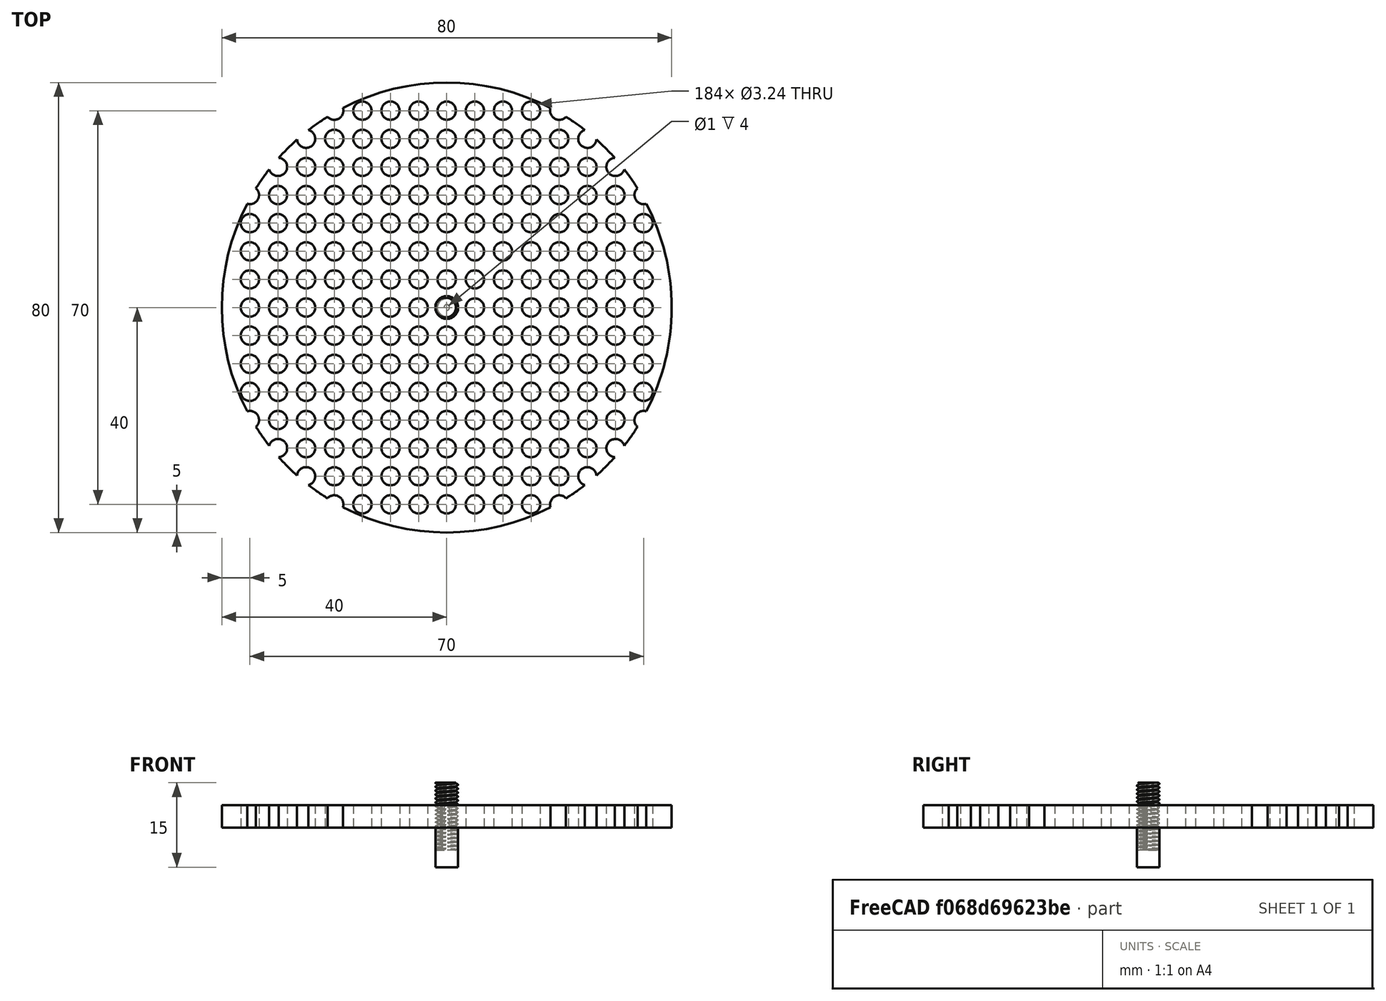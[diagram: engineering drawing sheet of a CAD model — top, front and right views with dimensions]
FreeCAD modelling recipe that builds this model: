
FCSTD DOCUMENT  (FreeCAD 0.21R0.21.2)
Label: XL30SampleholderBreadboard2
License: All rights reserved
LicenseURL: https://en.wikipedia.org/wiki/All_rights_reserved
objects: Part::Cylinder×4, Part::FeaturePython×3, Part::Cut×3, Part::MultiFuse×2, Spreadsheet::Sheet×1
note: 11 computed .brp shape members not serialized (recipe doc carries the construction recipe); baked Part::Feature solids carry a one-line shape summary decoded from their .brp

FEATURE [Spreadsheet::Sheet] Spreadsheet  label="BreadboardConfig"
  cells = A1='Parameters; E1='Calculated properties; A2='Diameter of stage; B2(dia_breadboard)=80; C2='The outer diameter of the breadboard stage; E2='Number of elements per diameter; F2(nElements)==floor((dia_breadboard - matrix_screw_m) / d_hole); A3='Thickness of the breadboard; B3(t_plat)=4; C3='The thickness of the breadboard; A5='Screw matrix parameters; A6='Screw major diameter; B6(matrix_screw_m)=4; C6='Screw major diameter; A7='Screw pitch; B7(matrix_screw_pitch)=0.7; C7='Pitch has to match screw major diameter; A8='Hole spacing; B8(d_hole)=5; C8='Spacing between holes
FEATURE [Part::Cylinder] Cylinder
  Angle = 360
  AttacherType = Attacher::AttachEngine3D
  FirstAngle = 0
  Height = 7
  Placement = pos=(0,0,-7) rot=(0,0,1;0rad)
  Radius = 2
  SecondAngle = 0
FEATURE [Part::Cylinder] Cylinder001
  Angle = 360
  AttacherType = Attacher::AttachEngine3D
  FirstAngle = 0
  Height = 4
  Radius = 40
  SecondAngle = 0
  expr: Height = <<BreadboardConfig>>.t_plat
  expr: Radius = <<BreadboardConfig>>.dia_breadboard / 2
FEATURE [Part::FeaturePython] ScrewTap  label="M4x7-ScrewTap"  # Fasteners workbench fastener (typed FeaturePython)
  diameter = 6
  diameterCustom = 7
  invert = false
  leftHanded = false
  length = 7
  matchOuter = false
  offset = 0
  pitchCustom = 1
  thread = false
  type = 0
FEATURE [Part::Cut] Cut  label="M4Adapter"
  Base = -> Cylinder
  Tool = -> ScrewTap
FEATURE [Part::FeaturePython] ScrewTap001  label="4x12-ScrewTap"  # Fasteners workbench fastener (typed FeaturePython)
  Placement = pos=(0,0,8) rot=(0,0,1;0rad)
  diameter = 29
  diameterCustom = 4
  invert = false
  leftHanded = false
  length = 12
  matchOuter = false
  offset = 0
  pitchCustom = 0.7
  thread = true
  type = 2
  expr: .Placement.Base.z = <<BreadboardConfig>>.t_plat * 2
  expr: diameterCustom = <<BreadboardConfig>>.matrix_screw_m
  expr: length = <<BreadboardConfig>>.t_plat * 3
  expr: pitchCustom = <<BreadboardConfig>>.matrix_screw_pitch
FEATURE [Part::FeaturePython] Array  # Draft array (typed FeaturePython)
  AlwaysSyncPlacement = false
  Angle = 360
  ArrayType = 0
  Axis = (0,0,1)
  Base = -> ScrewTap001
  Center = (0,0,0)
  Count = 225
  ExpandArray = false
  Fuse = false
  IntervalAxis = (0,0,0)
  IntervalX = (5,0,0)
  IntervalY = (0,5,0)
  IntervalZ = (0,0,10)
  NumberCircles = 3
  NumberPolar = 5
  NumberX = 15
  NumberY = 15
  NumberZ = 1
  Placement = pos=(-35,-35,0) rot=(0,0,1;0rad)
  PlacementList = 225 placements: [(0,0,8),(0,5,8),(0,10,8),(0,15,8),(0,20,8),(0,25,8),(0,30,8),(0,35,8),(0,40,8),(0,45,8),(0,50,8),(0,55,8),(0,60,8),(0,65,8),(0,70,8),(5,0,8),(5,5,8),(5,10,8),(5,15,8),(5,20,8),(5,25,8),(5,30,8),(5,35,8),(5,40,8),(5,45,8),(5,50,8),(5,55,8),(5,60,8),(5,65,8),(5,70,8),(10,0,8),(10,5,8),(10,10,8),(10,15,8),(10,20,8),(10,25,8),(10,30,8),(10,35,8),(10,40,8),(10,45,8),(10,50,8),(10,55,8),(10,60,8),+182 more]
  RadialDistance = 50
  ScaleList = (225) [(1,1,1),(1,1,1),(1,1,1),(1,1,1),(1,1,1),(1,1,1),(1,1,1),(1,1,1),(1,1,1),(1,1,1),(1,1,1),(1,1,1),(1,1,1),(1,1,1),(1,1,1),(1,1,1),(1,1,1),(1,1,1),+207 more]
  Symmetry = 1
  TangentialDistance = 25
  expr: .IntervalX.x = <<BreadboardConfig>>.d_hole
  expr: .IntervalY.y = <<BreadboardConfig>>.d_hole
  expr: .Placement.Base.x = -(<<BreadboardConfig>>.nElements - 1) / 2 * <<BreadboardConfig>>.d_hole
  expr: .Placement.Base.y = -(<<BreadboardConfig>>.nElements - 1) / 2 * <<BreadboardConfig>>.d_hole
  expr: NumberX = <<BreadboardConfig>>.nElements
  expr: NumberY = <<BreadboardConfig>>.nElements
FEATURE [Part::Cut] Cut001
  Base = -> Cylinder001
  Tool = -> Array
FEATURE [Part::Cylinder] Cylinder002  label="Fillingcenter"
  Angle = 360
  AttacherType = Attacher::AttachEngine3D
  FirstAngle = 0
  Height = 4
  Radius = 2.4
  SecondAngle = 0
  expr: Height = <<BreadboardConfig>>.t_plat
  expr: Radius = <<BreadboardConfig>>.matrix_screw_m / 2 * 1.2
FEATURE [Part::MultiFuse] Fusion  label="Breadboard"
  Shapes = -> [Cut001,Cylinder002]
FEATURE [Part::MultiFuse] Fusion001
  Shapes = -> [Cut,Fusion]
FEATURE [Part::Cylinder] Cylinder003  label="FaradayCup"
  Angle = 360
  AttacherType = Attacher::AttachEngine3D
  FirstAngle = 0
  Height = 4
  Radius = 0.5
  SecondAngle = 0
  expr: Height = <<BreadboardConfig>>.t_plat
FEATURE [Part::Cut] Cut002
  Base = -> Fusion001
  Tool = -> Cylinder003
